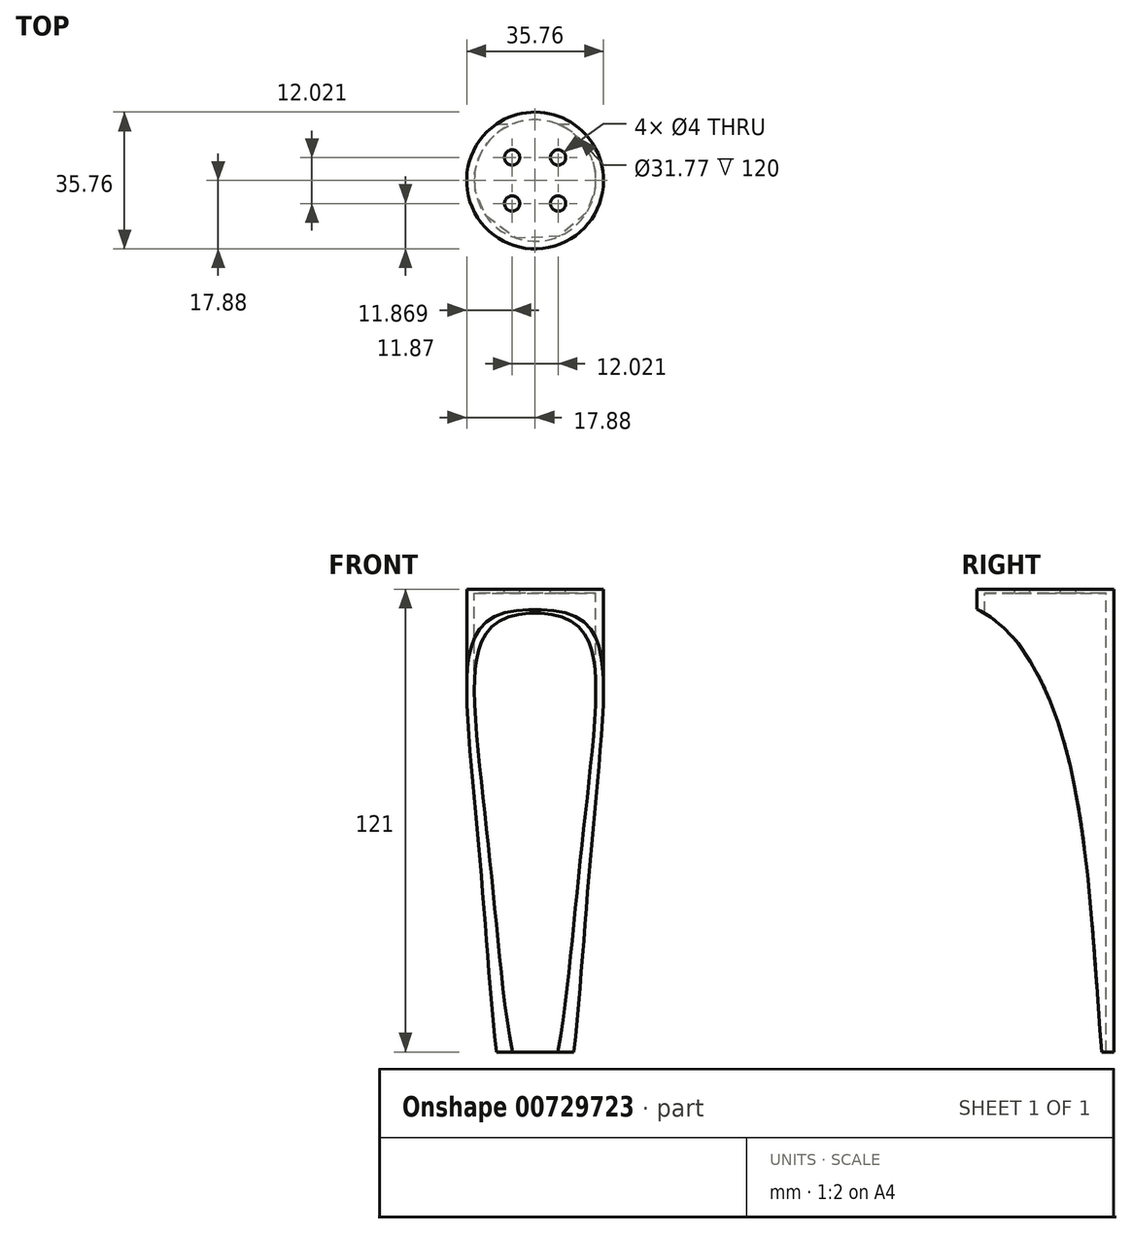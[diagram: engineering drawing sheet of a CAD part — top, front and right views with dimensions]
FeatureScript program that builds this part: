
annotation { "Feature Type Name" : "Feature", "Feature Type Description" : "" }
export const myFeature = defineFeature(function(context is Context, id is Id, definition is map)
    precondition{}
    {
        {
            var Q0;
            Q0=qCreatedBy(makeId("Top.planeOp"),FACE);
            var sketch = newSketch(context, id + "F0", { "sketchPlane" : qUnion([Q0])});
            skCircle(sketch, "E0", {"center": v(0, 0) * mm, "radius": 17.88 * mm});
            skSolve(sketch);
        }
        {
            var Q0;
            Q0=makeQuery(id+"F0.imprint","IMPRINT",FACE,{"disambiguationData":[TD([[makeQuery(id+"F0.imprint","IMPRINT",EDGE,{"derivedFrom":sQuery(id+"F0.wireOp",EDGE,"E0")}),1.0]])]});
            extrude(context, id + "F1", {"entities" : qUnion([Q0]), "depth" : 1 * mm, "offsetDistance" : 25 * mm});
        }
        {
            var Q0;
            Q0=makeQuery(id+"F1.opExtrude","CAP_FACE",FACE,{"disambiguationData":[OSD([sQuery(id+"F0.wireOp",EDGE,"E0")])],"isStart":true});
            var sketch = newSketch(context, id + "F2", { "sketchPlane" : qUnion([Q0])});
            skCircle(sketch, "E1", {"center": v(0, 0) * mm, "radius": 17.88 * mm});
            skCircle(sketch, "E2", {"center": v(0, 0) * mm, "radius": 15.88 * mm});
            skSolve(sketch);
        }
        {
            var Q0;
            Q0 = qSketchRegion(id + "F2", true);
            extrude(context, id + "F3", {"entities" : qUnion([Q0]), "operationType" : NewBodyOperationType.ADD, "depth" : 120 * mm, "offsetDistance" : 25 * mm});
        }
        {
            var Q0;
            Q0=qCreatedBy(makeId("Right.planeOp"),FACE);
            var sketch = newSketch(context, id + "F4", { "sketchPlane" : qUnion([Q0])});
            skFitSpline(sketch, "E3", {"points": [v(-23.55, -2.93) * mm, v(2.93, -32.7) * mm, v(15.18, -125.34) * mm], "startDerivative": vector(85.56, -4.52) * mm, "endDerivative": vector(13.72, -154.47) * mm});
            skLineSegment(sketch, "E4", {"start": v(-23.55, -2.93) * mm, "end": v(-23.55, -130.52) * mm});
            skLineSegment(sketch, "E5", {"start": v(-23.55, -130.52) * mm, "end": v(15.18, -125.34) * mm});
            skSolve(sketch);
        }
        {
            var Q0;
            Q0=makeQuery(id+"F4.imprint","IMPRINT",FACE,{"disambiguationData":[TD([[makeQuery(id+"F4.imprint","IMPRINT",EDGE,{"derivedFrom":sQuery(id+"F4.wireOp",EDGE,"E3")}),-1.0]])]});
            extrude(context, id + "F5", {"entities" : qUnion([Q0]), "operationType" : NewBodyOperationType.REMOVE, "endBound" : BoundingType.SYMMETRIC, "oppositeDirection" : true, "depth" : 200 * mm, "offsetDistance" : 25 * mm});
        }
        {
            var Q0;
            Q0=makeQuery(id+"F1.opExtrude","CAP_FACE",FACE,{"disambiguationData":[OSD([sQuery(id+"F0.wireOp",EDGE,"E0")])],"isStart":false});
            var sketch = newSketch(context, id + "F6", { "sketchPlane" : qUnion([Q0])});
            skCircle(sketch, "E6", {"center": v(0, 0) * mm, "radius": 8.5 * mm, "construction": true});
            skCircle(sketch, "E7", {"center": v(-6.01, 6.01) * mm, "radius": 2 * mm});
            skCircle(sketch, "E8", {"center": v(6.01, 6.01) * mm, "radius": 2 * mm});
            skCircle(sketch, "E9", {"center": v(6.01, -6.01) * mm, "radius": 2 * mm});
            skCircle(sketch, "E10", {"center": v(-6.01, -6.01) * mm, "radius": 2 * mm});
            skSolve(sketch);
        }
        {
            var Q0;
            Q0=makeQuery(id+"F6.imprint","IMPRINT",FACE,{"disambiguationData":[TD([[makeQuery(id+"F6.imprint","IMPRINT",EDGE,{"derivedFrom":sQuery(id+"F6.wireOp",EDGE,"E7")}),1.0]])]});
            var Q1;
            Q1=makeQuery(id+"F6.imprint","IMPRINT",FACE,{"disambiguationData":[TD([[makeQuery(id+"F6.imprint","IMPRINT",EDGE,{"derivedFrom":sQuery(id+"F6.wireOp",EDGE,"E8")}),1.0]])]});
            var Q2;
            Q2=makeQuery(id+"F6.imprint","IMPRINT",FACE,{"disambiguationData":[TD([[makeQuery(id+"F6.imprint","IMPRINT",EDGE,{"derivedFrom":sQuery(id+"F6.wireOp",EDGE,"E9")}),1.0]])]});
            var Q3;
            Q3=makeQuery(id+"F6.imprint","IMPRINT",FACE,{"disambiguationData":[TD([[makeQuery(id+"F6.imprint","IMPRINT",EDGE,{"derivedFrom":sQuery(id+"F6.wireOp",EDGE,"E10")}),1.0]])]});
            extrude(context, id + "F7", {"entities" : qUnion([Q0, Q1, Q2, Q3]), "operationType" : NewBodyOperationType.REMOVE, "endBound" : BoundingType.THROUGH_ALL, "oppositeDirection" : true, "depth" : 25 * mm, "offsetDistance" : 25 * mm});
        }
    });
